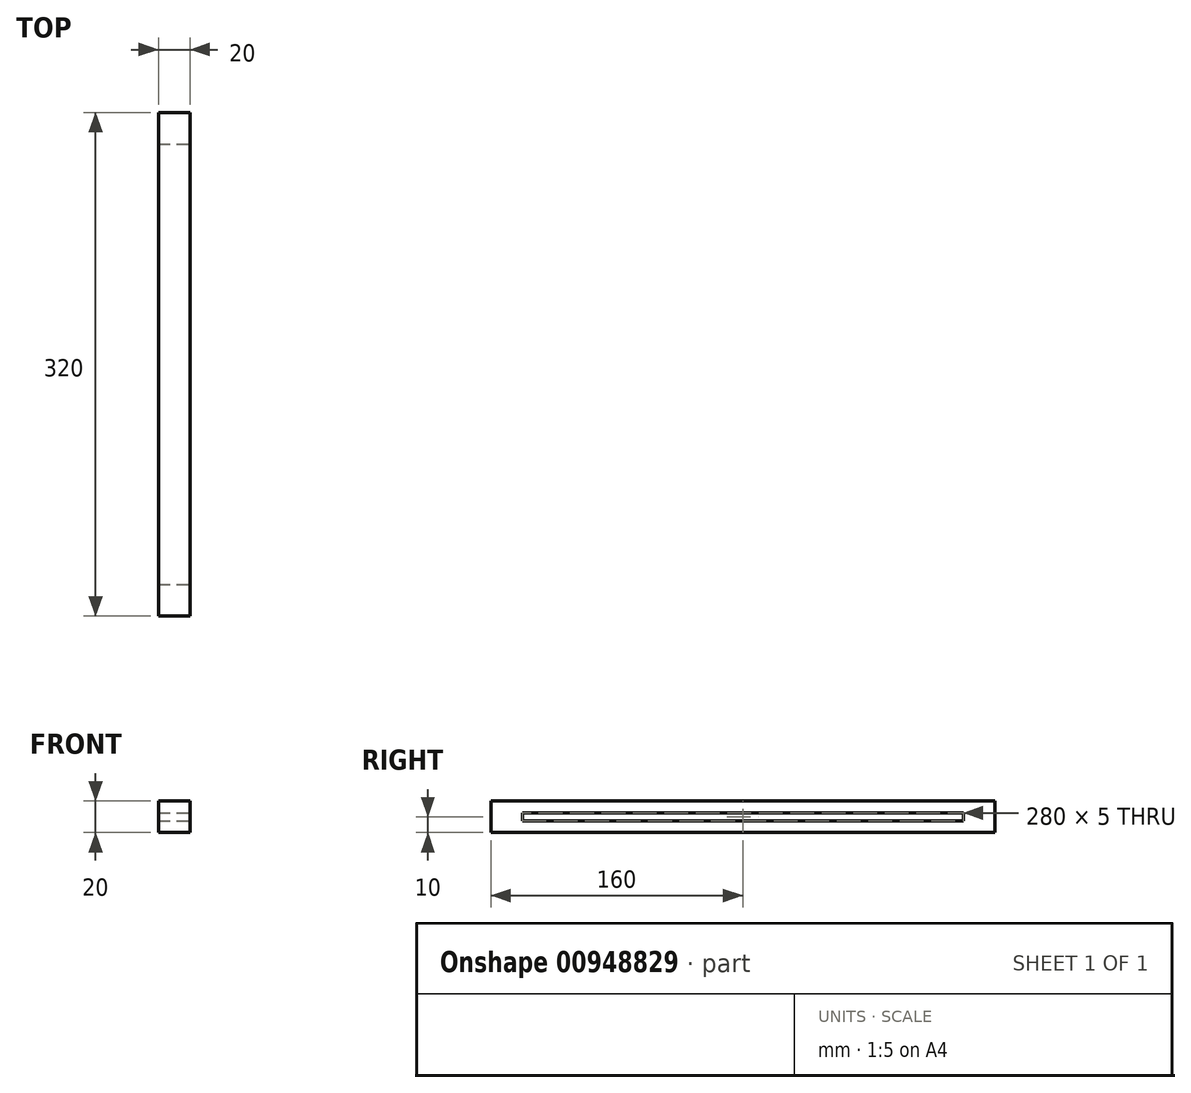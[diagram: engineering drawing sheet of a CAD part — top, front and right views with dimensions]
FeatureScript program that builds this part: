
annotation { "Feature Type Name" : "Feature", "Feature Type Description" : "" }
export const myFeature = defineFeature(function(context is Context, id is Id, definition is map)
    precondition{}
    {
        {
            var Q0;
            Q0=qCreatedBy(makeId("Front.planeOp"),FACE);
            var sketch = newSketch(context, id + "F0", { "sketchPlane" : qUnion([Q0])});
            skLineSegment(sketch, "E0.bottom", {"start": v(10, -10) * mm, "end": v(-10, -10) * mm});
            skLineSegment(sketch, "E0.top", {"start": v(10, 10) * mm, "end": v(-10, 10) * mm});
            skLineSegment(sketch, "E0.left", {"start": v(10, -10) * mm, "end": v(10, 10) * mm});
            skLineSegment(sketch, "E0.right", {"start": v(-10, -10) * mm, "end": v(-10, 10) * mm});
            skPoint(sketch, "E0.middle", {"position": v(0, 0) * mm});
            skSolve(sketch);
        }
        {
            var Q0;
            Q0=qSketchRegion(id+"F0",true);
            extrude(context, id + "F1", {"entities" : qUnion([Q0]), "endBound" : BoundingType.SYMMETRIC, "depth" : 320 * mm, "offsetDistance" : 25 * mm});
        }
        {
            var Q0;
            Q0=makeQuery(id+"F1.opExtrude","SWEPT_FACE",FACE,{"disambiguationData":[OSD([sQuery(id+"F0.wireOp",EDGE,"E0.left")])]});
            var sketch = newSketch(context, id + "F2", { "sketchPlane" : qUnion([Q0])});
            skLineSegment(sketch, "E1.bottom", {"start": v(140, -2.5) * mm, "end": v(-140, -2.5) * mm});
            skLineSegment(sketch, "E1.top", {"start": v(140, 2.5) * mm, "end": v(-140, 2.5) * mm});
            skLineSegment(sketch, "E1.left", {"start": v(140, -2.5) * mm, "end": v(140, 2.5) * mm});
            skLineSegment(sketch, "E1.right", {"start": v(-140, -2.5) * mm, "end": v(-140, 2.5) * mm});
            skPoint(sketch, "E1.middle", {"position": v(0, 0) * mm});
            skSolve(sketch);
        }
        {
            var Q0;
            Q0=qSketchRegion(id+"F2",true);
            extrude(context, id + "F3", {"entities" : qUnion([Q0]), "operationType" : NewBodyOperationType.REMOVE, "oppositeDirection" : true, "depth" : 25 * mm, "offsetDistance" : 25 * mm});
        }
    });
